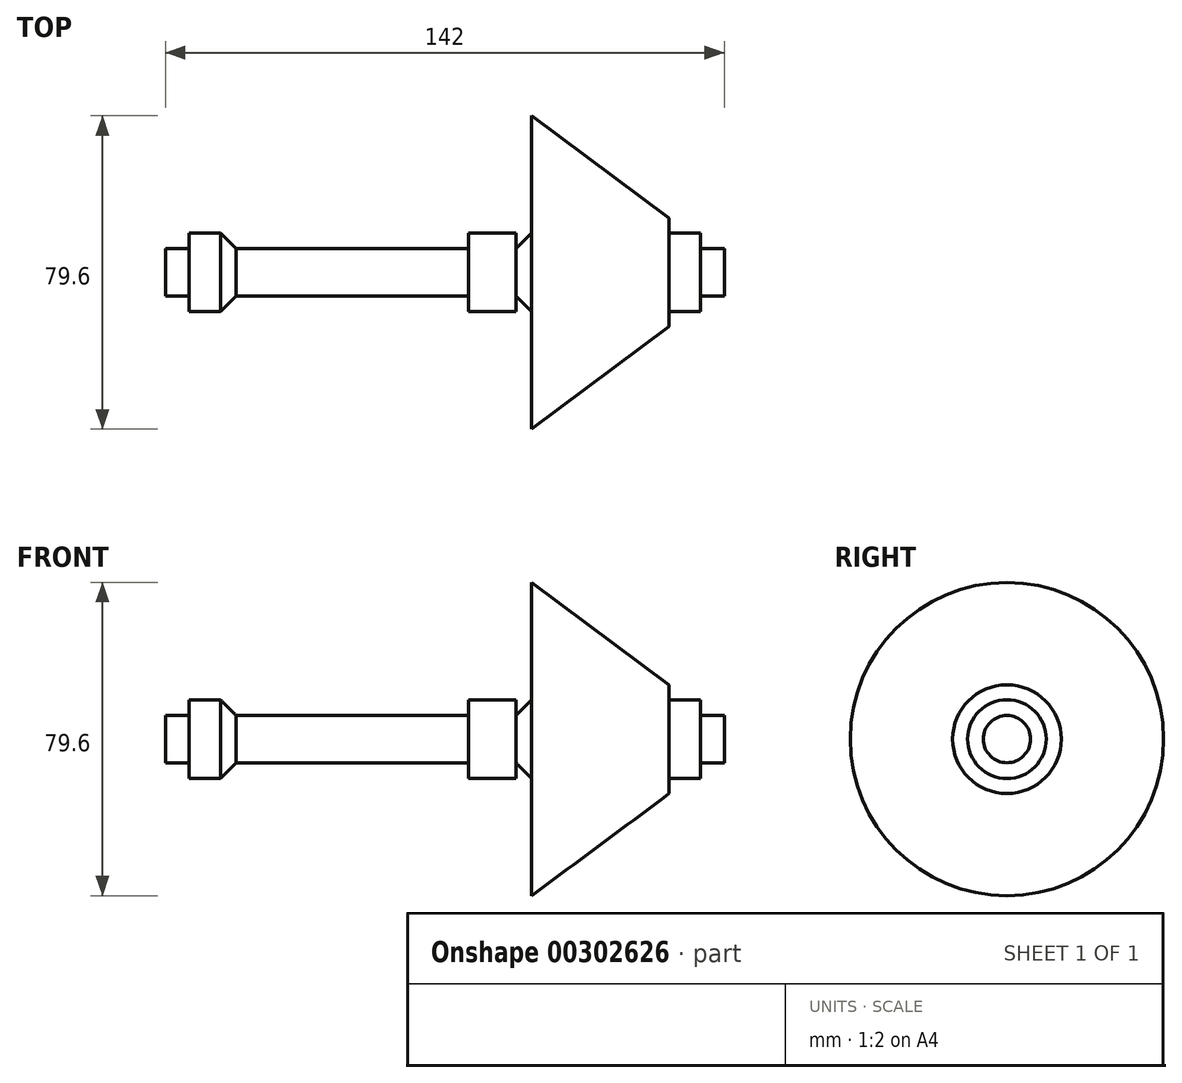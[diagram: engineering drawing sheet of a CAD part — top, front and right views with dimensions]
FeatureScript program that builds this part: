
annotation { "Feature Type Name" : "Feature", "Feature Type Description" : "" }
export const myFeature = defineFeature(function(context is Context, id is Id, definition is map)
    precondition{}
    {
        {
            var Q0;
            Q0=qCreatedBy(makeId("Right.planeOp"),FACE);
            var sketch = newSketch(context, id + "F0", { "sketchPlane" : qUnion([Q0])});
            skCircle(sketch, "E0", {"center": v(0, 0) * mm, "radius": 6 * mm});
            skSolve(sketch);
        }
        {
            var Q0;
            Q0 = qSketchRegion(id + "F0", true);
            extrude(context, id + "F1", {"entities" : qUnion([Q0]), "endBound" : BoundingType.SYMMETRIC, "depth" : 142 * mm});
        }
        {
            var Q0;
            Q0=qCreatedBy(makeId("Top.planeOp"),FACE);
            var sketch = newSketch(context, id + "F2", { "sketchPlane" : qUnion([Q0])});
            skLineSegment(sketch, "E1", {"start": v(0, 0) * mm, "end": v(65, 0) * mm});
            skLineSegment(sketch, "E2", {"start": v(0, 0) * mm, "end": v(-65, 0) * mm});
            skLineSegment(sketch, "E3", {"start": v(22.05, 0) * mm, "end": v(57, 0) * mm});
            skLineSegment(sketch, "E4", {"start": v(57, 0) * mm, "end": v(57, 13.8) * mm});
            skLineSegment(sketch, "E5", {"start": v(22.05, 0) * mm, "end": v(22.05, 39.8) * mm});
            skLineSegment(sketch, "E6", {"start": v(22.05, 39.8) * mm, "end": v(57, 13.8) * mm});
            skLineSegment(sketch, "E7.bottom", {"start": v(-65, 0) * mm, "end": v(-57, 0) * mm});
            skLineSegment(sketch, "E7.top", {"start": v(-65, 10) * mm, "end": v(-57, 10) * mm});
            skLineSegment(sketch, "E7.left", {"start": v(-65, 0) * mm, "end": v(-65, 10) * mm});
            skLineSegment(sketch, "E7.right", {"start": v(-57, 0) * mm, "end": v(-57, 10) * mm});
            skLineSegment(sketch, "E8.bottom", {"start": v(65, 0) * mm, "end": v(57, 0) * mm});
            skLineSegment(sketch, "E8.top", {"start": v(65, 10) * mm, "end": v(57, 10) * mm});
            skLineSegment(sketch, "E8.left", {"start": v(65, 0) * mm, "end": v(65, 10) * mm});
            skLineSegment(sketch, "E8.right", {"start": v(57, 0) * mm, "end": v(57, 10) * mm});
            skLineSegment(sketch, "E9", {"start": v(-57, 10) * mm, "end": v(-47, 0) * mm});
            skLineSegment(sketch, "E10", {"start": v(22.05, 0) * mm, "end": v(22.05, 10) * mm});
            skLineSegment(sketch, "E11", {"start": v(22.05, 10) * mm, "end": v(12.05, 0) * mm});
            skLineSegment(sketch, "E12.bottom", {"start": v(12.05, 0) * mm, "end": v(0, 0) * mm});
            skLineSegment(sketch, "E13.bottom", {"start": v(18.02, 10) * mm, "end": v(5.97, 10) * mm});
            skLineSegment(sketch, "E13.top", {"start": v(18.02, 0) * mm, "end": v(5.97, 0) * mm});
            skLineSegment(sketch, "E13.left", {"start": v(18.02, 10) * mm, "end": v(18.02, 0) * mm});
            skLineSegment(sketch, "E13.right", {"start": v(5.97, 10) * mm, "end": v(5.97, 0) * mm});
            skSolve(sketch);
        }
        {
            var Q0;
            Q0 = qSketchRegion(id + "F2", true);
            var Q1;
            Q1=sQuery(id+"F2.wireOp",EDGE,"E2");
            revolve(context, id + "F3", {"operationType" : NewBodyOperationType.ADD, "entities" : qUnion([Q0]), "axis" : qUnion([Q1]), "revolveType" : RevolveType.FULL});
        }
    });
